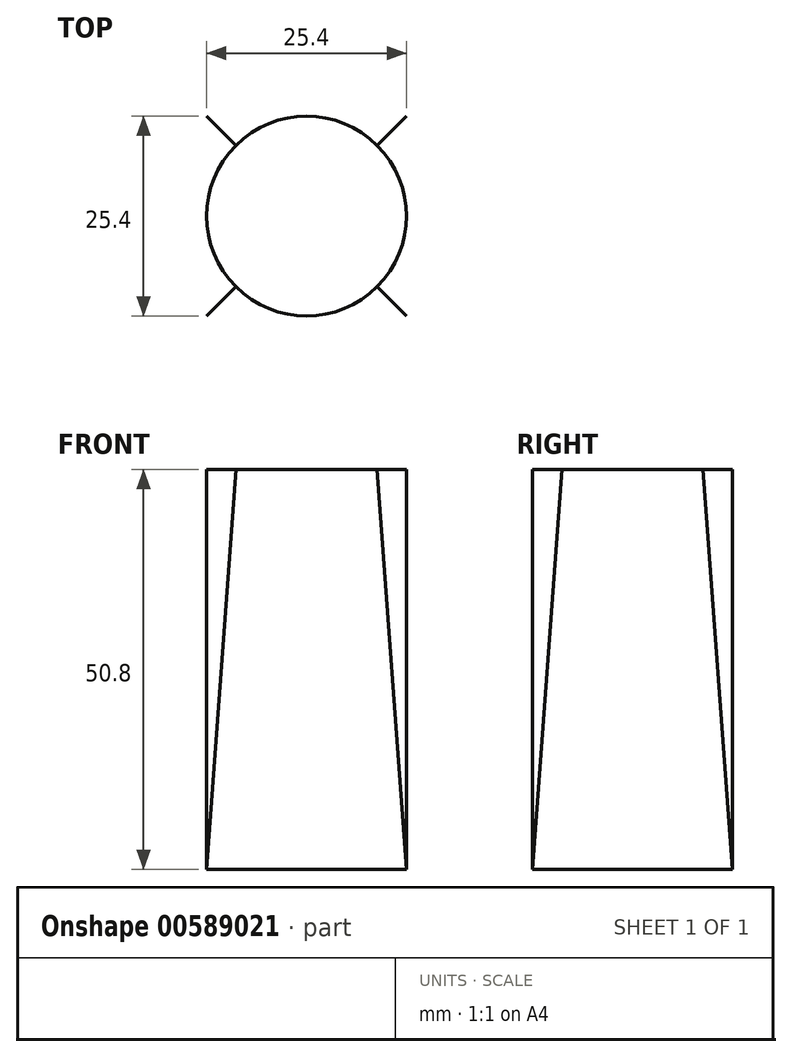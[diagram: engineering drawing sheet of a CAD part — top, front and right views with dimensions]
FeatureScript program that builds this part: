
annotation { "Feature Type Name" : "Feature", "Feature Type Description" : "" }
export const myFeature = defineFeature(function(context is Context, id is Id, definition is map)
    precondition{}
    {
        {
            var Q0;
            Q0=qCreatedBy(makeId("Top.planeOp"),FACE);
            var sketch = newSketch(context, id + "F0", { "sketchPlane" : qUnion([Q0])});
            skLineSegment(sketch, "E0.bottom", {"start": v(0, 39.66) * mm, "end": v(25.4, 39.66) * mm});
            skLineSegment(sketch, "E0.top", {"start": v(0, 14.26) * mm, "end": v(25.4, 14.26) * mm});
            skLineSegment(sketch, "E0.left", {"start": v(0, 39.66) * mm, "end": v(0, 14.26) * mm});
            skLineSegment(sketch, "E0.right", {"start": v(25.4, 39.66) * mm, "end": v(25.4, 14.26) * mm});
            skLineSegment(sketch, "E1.bottom", {"start": v(25.4, 39.66) * mm, "end": v(25.4, 39.66) * mm});
            skLineSegment(sketch, "E1.top", {"start": v(25.4, 14.26) * mm, "end": v(25.4, 14.26) * mm});
            skSolve(sketch);
        }
        {
            var Q0;
            Q0=qCreatedBy(makeId("Top.planeOp"),FACE);
            cPlane(context, id + "F1", {"entities" : qUnion([Q0]), "cplaneType" : CPlaneType.OFFSET, "offset" : 50.8 * mm, "width" : 152.4 * mm, "height" : 152.4 * mm});
        }
        {
            var Q0;
            Q0=qCreatedBy(id+"F1.planeOp",FACE);
            var sketch = newSketch(context, id + "F2", { "sketchPlane" : qUnion([Q0])});
            skCircle(sketch, "E2", {"center": v(12.7, 26.96) * mm, "radius": 12.7 * mm});
            skSolve(sketch);
        }
        {
            var Q0;
            Q0=makeQuery(id+"F2.imprint","IMPRINT",FACE,{"disambiguationData":[TD([[makeQuery(id+"F2.imprint","IMPRINT",EDGE,{"derivedFrom":sQuery(id+"F2.wireOp",EDGE,"E2")}),1.0]])]});
            var Q1;
            Q1=makeQuery(id+"F0.imprint","IMPRINT",FACE,{"disambiguationData":[TD([[makeQuery(id+"F0.imprint","IMPRINT",EDGE,{"derivedFrom":sQuery(id+"F0.wireOp",EDGE,"E0.bottom")}),-1.0]])]});
            loft(context, id + "F3", {"sheetProfilesArray" : [{ "sheetProfileEntities" : qUnion([Q0]) }, { "sheetProfileEntities" : qUnion([Q1]) }]});
        }
    });
